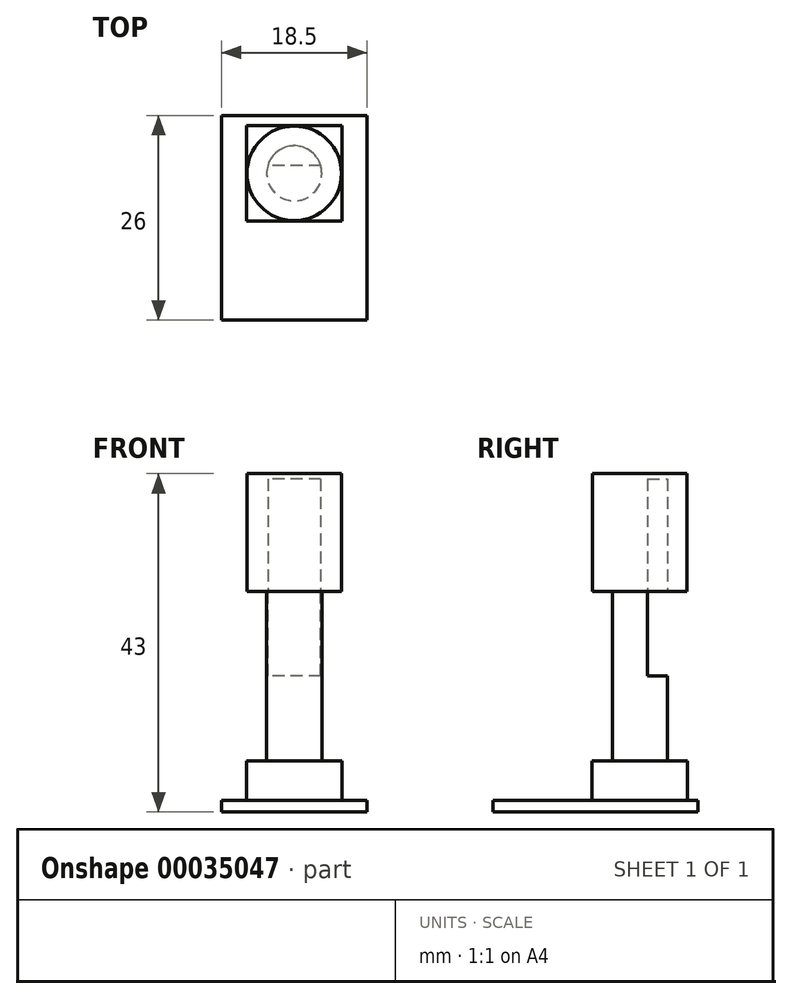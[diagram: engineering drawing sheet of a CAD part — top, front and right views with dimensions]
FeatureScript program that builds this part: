
annotation { "Feature Type Name" : "Feature", "Feature Type Description" : "" }
export const myFeature = defineFeature(function(context is Context, id is Id, definition is map)
    precondition{}
    {
        {
            var Q0;
            Q0=qCreatedBy(makeId("Top.planeOp"),FACE);
            var sketch = newSketch(context, id + "F0", { "sketchPlane" : qUnion([Q0])});
            skLineSegment(sketch, "E0.rect.bottom", {"start": v(9.25, -13) * mm, "end": v(-9.25, -13) * mm});
            skLineSegment(sketch, "E0.rect.top", {"start": v(9.25, 13) * mm, "end": v(-9.25, 13) * mm});
            skLineSegment(sketch, "E0.rect.left", {"start": v(9.25, -13) * mm, "end": v(9.25, 13) * mm});
            skLineSegment(sketch, "E0.rect.right", {"start": v(-9.25, -13) * mm, "end": v(-9.25, 13) * mm});
            skPoint(sketch, "E0.rect.middle", {"position": v(0, 0) * mm});
            skSolve(sketch);
        }
        {
            var Q0;
            Q0 = qSketchRegion(id + "F0", true);
            extrude(context, id + "F1", {"entities" : qUnion([Q0]), "depth" : 1.5 * mm});
        }
        {
            var Q0;
            Q0=makeQuery(id+"F1.opExtrude","CAP_FACE",FACE,{"disambiguationData":[OSD([sQuery(id+"F0.wireOp",EDGE,"E0.rect.bottom"),sQuery(id+"F0.wireOp",EDGE,"E0.rect.top"),sQuery(id+"F0.wireOp",EDGE,"E0.rect.left"),sQuery(id+"F0.wireOp",EDGE,"E0.rect.right")])],"isStart":false});
            var sketch = newSketch(context, id + "F2", { "sketchPlane" : qUnion([Q0])});
            skLineSegment(sketch, "E1.rect.bottom", {"start": v(6.05, -0.4) * mm, "end": v(-6.05, -0.4) * mm});
            skLineSegment(sketch, "E1.rect.top", {"start": v(6.05, 11.7) * mm, "end": v(-6.05, 11.7) * mm});
            skLineSegment(sketch, "E1.rect.left", {"start": v(6.05, -0.4) * mm, "end": v(6.05, 11.7) * mm});
            skLineSegment(sketch, "E1.rect.right", {"start": v(-6.05, -0.4) * mm, "end": v(-6.05, 11.7) * mm});
            skPoint(sketch, "E1.rect.middle", {"position": v(0, 5.64) * mm});
            skSolve(sketch);
        }
        {
            var Q0;
            Q0 = qSketchRegion(id + "F2", true);
            extrude(context, id + "F3", {"entities" : qUnion([Q0]), "operationType" : NewBodyOperationType.ADD, "depth" : 5 * mm});
        }
        {
            var Q0;
            Q0=makeQuery(id+"F3.opExtrude","CAP_FACE",FACE,{"disambiguationData":[OSD([sQuery(id+"F2.wireOp",EDGE,"E1.rect.bottom"),sQuery(id+"F2.wireOp",EDGE,"E1.rect.top"),sQuery(id+"F2.wireOp",EDGE,"E1.rect.left"),sQuery(id+"F2.wireOp",EDGE,"E1.rect.right")])],"isStart":false});
            var sketch = newSketch(context, id + "F4", { "sketchPlane" : qUnion([Q0])});
            skCircle(sketch, "E2", {"center": v(0, 5.64) * mm, "radius": 3.5 * mm});
            skPoint(sketch, "E2.centerSnap0", {"position": v(6.05, 5.64) * mm});
            skSolve(sketch);
        }
        {
            var Q0;
            Q0 = qSketchRegion(id + "F4", true);
            extrude(context, id + "F5", {"entities" : qUnion([Q0]), "operationType" : NewBodyOperationType.ADD, "depth" : 21.5 * mm});
        }
        {
            var Q0;
            Q0=makeQuery(id+"F5.opExtrude","CAP_FACE",FACE,{"disambiguationData":[OSD([sQuery(id+"F4.wireOp",EDGE,"E2")])],"isStart":false});
            var sketch = newSketch(context, id + "F6", { "sketchPlane" : qUnion([Q0])});
            skLineSegment(sketch, "E3", {"start": v(0, 2.14) * mm, "end": v(0, 6.64) * mm});
            skLineSegment(sketch, "E4", {"start": v(0, 6.64) * mm, "end": v(-3.35, 6.64) * mm});
            skLineSegment(sketch, "E5", {"start": v(0, 6.64) * mm, "end": v(3.35, 6.64) * mm});
            skSolve(sketch);
        }
        {
            var Q0;
            Q0 = qSketchRegion(id + "F6", true);
            var Q1;
            {var subQ2=sQuery(id+"F6.wireOp",EDGE,"E4");Q1=makeQuery(id+"F6.imprint","IMPRINT",FACE,{"disambiguationData":[TD([[makeQuery(id+"F6.imprint","IMPRINT",EDGE,{"derivedFrom":subQ2}),-1.0]])]});}
            extrude(context, id + "F7", {"entities" : qUnion([Q0, Q1]), "operationType" : NewBodyOperationType.REMOVE, "oppositeDirection" : true, "depth" : 10.7 * mm});
        }
        {
            var Q0;
            Q0=makeQuery(id+"F5.opExtrude","CAP_FACE",FACE,{"disambiguationData":[OSD([sQuery(id+"F4.wireOp",EDGE,"E2")])],"isStart":false});
            var sketch = newSketch(context, id + "F8", { "sketchPlane" : qUnion([Q0])});
            skCircle(sketch, "E6", {"center": v(0, 5.64) * mm, "radius": 6 * mm});
            skSolve(sketch);
        }
        {
            var Q0;
            Q0 = qSketchRegion(id + "F8", true);
            extrude(context, id + "F9", {"entities" : qUnion([Q0]), "operationType" : NewBodyOperationType.ADD, "depth" : 15 * mm});
        }
        {
            var Q0;
            Q0=makeQuery(id+"F7.boolean.opBoolean","COPY",FACE,{"derivedFrom":makeQuery(id+"F7.opExtrude","CAP_FACE",FACE,{"disambiguationData":[OSD([sQuery(id+"F4.wireOp",EDGE,"E2"),sQuery(id+"F6.wireOp",EDGE,"E4"),sQuery(id+"F6.wireOp",EDGE,"E5")])],"isStart":false})});
            extrude(context, id + "F10", {"entities" : qUnion([Q0]), "operationType" : NewBodyOperationType.REMOVE, "depth" : 25 * mm});
        }
    });
